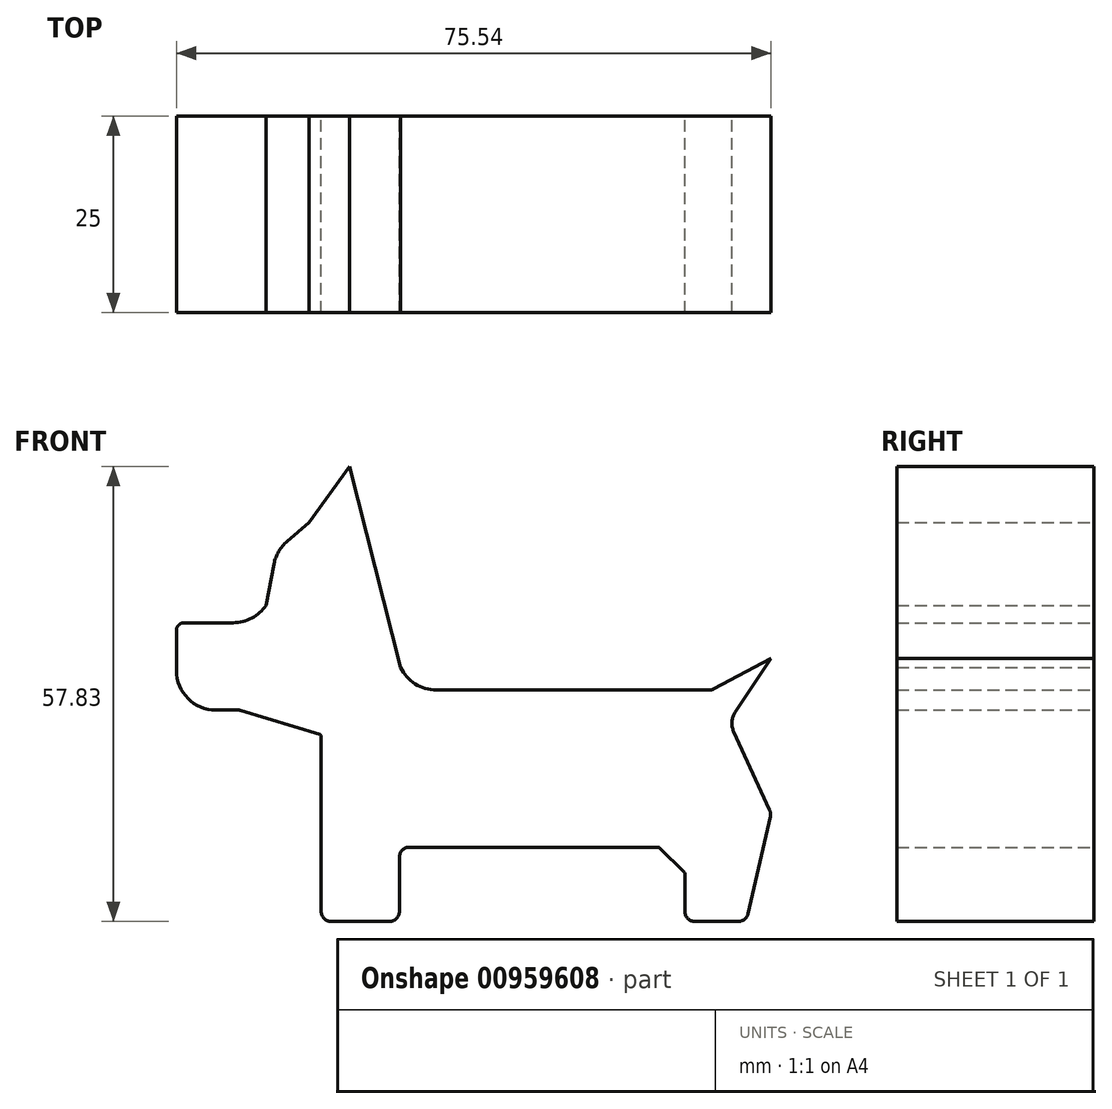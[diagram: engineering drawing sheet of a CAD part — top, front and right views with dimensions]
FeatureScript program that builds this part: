
annotation { "Feature Type Name" : "Feature", "Feature Type Description" : "" }
export const myFeature = defineFeature(function(context is Context, id is Id, definition is map)
    precondition{}
    {
        {
            var Q0;
            Q0=qCreatedBy(makeId("Front.planeOp"),FACE);
            var sketch = newSketch(context, id + "F0", { "sketchPlane" : qUnion([Q0])});
            skLineSegment(sketch, "E0", {"start": v(-49.26, 2.66) * mm, "end": v(-49.26, -1.54) * mm});
            skLineSegment(sketch, "E1", {"start": v(-44.26, -6.54) * mm, "end": v(-41.47, -6.54) * mm});
            skLineSegment(sketch, "E2", {"start": v(-41.1, -6.6) * mm, "end": v(-31.05, -9.66) * mm});
            skLineSegment(sketch, "E3", {"start": v(-30.87, -9.9) * mm, "end": v(-30.87, -32.14) * mm});
            skLineSegment(sketch, "E4", {"start": v(-29.6, -33.4) * mm, "end": v(-22.21, -33.4) * mm});
            skLineSegment(sketch, "E5", {"start": v(-20.94, -32.14) * mm, "end": v(-20.94, -25.24) * mm});
            skLineSegment(sketch, "E6", {"start": v(-19.67, -23.97) * mm, "end": v(11.94, -23.97) * mm});
            skLineSegment(sketch, "E7", {"start": v(12.12, -24.04) * mm, "end": v(15.25, -27.17) * mm});
            skLineSegment(sketch, "E8", {"start": v(15.32, -27.35) * mm, "end": v(15.32, -32.14) * mm});
            skLineSegment(sketch, "E9", {"start": v(16.6, -33.4) * mm, "end": v(22.1, -33.4) * mm});
            skLineSegment(sketch, "E10", {"start": v(23.34, -32.42) * mm, "end": v(26.17, -20.03) * mm});
            skLineSegment(sketch, "E11", {"start": v(26.09, -19.22) * mm, "end": v(21.52, -9.26) * mm});
            skLineSegment(sketch, "E12", {"start": v(21.71, -6.83) * mm, "end": v(26.27, 0) * mm});
            skLineSegment(sketch, "E13", {"start": v(26.27, 0) * mm, "end": v(18.98, -3.88) * mm});
            skPoint(sketch, "E13.endSnap0", {"position": v(23.6, -4) * mm});
            skLineSegment(sketch, "E14", {"start": v(18.51, -4) * mm, "end": v(-16.26, -4) * mm});
            skLineSegment(sketch, "E15", {"start": v(-42.04, 4.54) * mm, "end": v(-48.27, 4.54) * mm});
            skLineSegment(sketch, "E16", {"start": v(-49.27, 3.54) * mm, "end": v(-49.26, 2.66) * mm});
            skPoint(sketch, "E17.visualSharp", {"position": v(-20.94, -23.97) * mm});
            skArc(sketch, "E17.filletArc", {"start": v(-19.67, -23.97) * mm, "mid": v(-20.57, -24.34) * mm, "end": v(-20.94, -25.24) * mm});
            skPoint(sketch, "E18.visualSharp", {"position": v(12.05, -23.97) * mm});
            skArc(sketch, "E18.filletArc", {"start": v(12.12, -24.04) * mm, "mid": v(12.04, -23.99) * mm, "end": v(11.94, -23.97) * mm});
            skPoint(sketch, "E19.visualSharp", {"position": v(15.32, -27.24) * mm});
            skArc(sketch, "E19.filletArc", {"start": v(15.32, -27.35) * mm, "mid": v(15.3, -27.25) * mm, "end": v(15.25, -27.17) * mm});
            skPoint(sketch, "E20.visualSharp", {"position": v(15.32, -33.4) * mm});
            skArc(sketch, "E20.filletArc", {"start": v(15.32, -32.14) * mm, "mid": v(15.7, -33.04) * mm, "end": v(16.6, -33.4) * mm});
            skPoint(sketch, "E21.visualSharp", {"position": v(23.12, -33.4) * mm});
            skArc(sketch, "E21.filletArc", {"start": v(22.1, -33.4) * mm, "mid": v(22.9, -33.13) * mm, "end": v(23.34, -32.42) * mm});
            skPoint(sketch, "E22.visualSharp", {"position": v(26.27, -19.6) * mm});
            skArc(sketch, "E22.filletArc", {"start": v(26.17, -20.03) * mm, "mid": v(26.2, -19.62) * mm, "end": v(26.09, -19.22) * mm});
            skPoint(sketch, "E23.visualSharp", {"position": v(-17.07, -4) * mm});
            skArc(sketch, "E23.filletArc", {"start": v(-20.79, -1.12) * mm, "mid": v(-18.94, -3.21) * mm, "end": v(-16.26, -4) * mm});
            skPoint(sketch, "E24.visualSharp", {"position": v(-30.87, -33.4) * mm});
            skArc(sketch, "E24.filletArc", {"start": v(-30.87, -32.14) * mm, "mid": v(-30.5, -33.04) * mm, "end": v(-29.6, -33.4) * mm});
            skPoint(sketch, "E25.visualSharp", {"position": v(-20.94, -33.4) * mm});
            skArc(sketch, "E25.filletArc", {"start": v(-22.21, -33.4) * mm, "mid": v(-21.31, -33.04) * mm, "end": v(-20.94, -32.14) * mm});
            skPoint(sketch, "E26.visualSharp", {"position": v(-30.87, -9.71) * mm});
            skArc(sketch, "E26.filletArc", {"start": v(-30.87, -9.9) * mm, "mid": v(-30.92, -9.75) * mm, "end": v(-31.05, -9.66) * mm});
            skPoint(sketch, "E27.visualSharp", {"position": v(-41.28, -6.54) * mm});
            skArc(sketch, "E27.filletArc", {"start": v(-41.1, -6.6) * mm, "mid": v(-41.28, -6.55) * mm, "end": v(-41.47, -6.54) * mm});
            skPoint(sketch, "E28.visualSharp", {"position": v(-49.26, -6.54) * mm});
            skArc(sketch, "E28.filletArc", {"start": v(-49.26, -1.54) * mm, "mid": v(-47.8, -5.08) * mm, "end": v(-44.26, -6.54) * mm});
            skPoint(sketch, "E29.visualSharp", {"position": v(-49.28, 4.54) * mm});
            skArc(sketch, "E29.filletArc", {"start": v(-48.27, 4.54) * mm, "mid": v(-48.98, 4.25) * mm, "end": v(-49.27, 3.54) * mm});
            skPoint(sketch, "E30.visualSharp", {"position": v(-39.37, 4.54) * mm});
            skArc(sketch, "E30.filletArc", {"start": v(-42.04, 4.54) * mm, "mid": v(-39.68, 5.14) * mm, "end": v(-37.88, 6.77) * mm});
            skPoint(sketch, "E31.visualSharp", {"position": v(-29.63, 19.15) * mm});
            skPoint(sketch, "E32.visualSharp", {"position": v(20.94, -7.99) * mm});
            skArc(sketch, "E32.filletArc", {"start": v(21.71, -6.83) * mm, "mid": v(21.3, -8.02) * mm, "end": v(21.52, -9.26) * mm});
            skPoint(sketch, "E33.visualSharp", {"position": v(18.76, -4) * mm});
            skArc(sketch, "E33.filletArc", {"start": v(18.51, -4) * mm, "mid": v(18.75, -3.96) * mm, "end": v(18.98, -3.88) * mm});
            skPoint(sketch, "E34.end.orphan", {"position": v(-30.87, 25.42) * mm});
            skLineSegment(sketch, "E35", {"start": v(-27.25, 24.42) * mm, "end": v(-20.79, -1.12) * mm});
            skLineSegment(sketch, "E36", {"start": v(-37.88, 6.77) * mm, "end": v(-36.87, 12.03) * mm});
            skLineSegment(sketch, "E37", {"start": v(-35.2, 14.89) * mm, "end": v(-32.41, 17.26) * mm});
            skLineSegment(sketch, "E38", {"start": v(-32.41, 17.26) * mm, "end": v(-27.25, 24.42) * mm});
            skPoint(sketch, "E39.visualSharp", {"position": v(-36.53, 13.75) * mm});
            skArc(sketch, "E39.filletArc", {"start": v(-35.2, 14.89) * mm, "mid": v(-36.28, 13.6) * mm, "end": v(-36.87, 12.03) * mm});
            skSolve(sketch);
        }
        {
            var Q0;
            Q0 = qSketchRegion(id + "F0", true);
            extrude(context, id + "F1", {"entities" : qUnion([Q0]), "depth" : 25 * mm, "offsetDistance" : 25 * mm});
        }
    });
